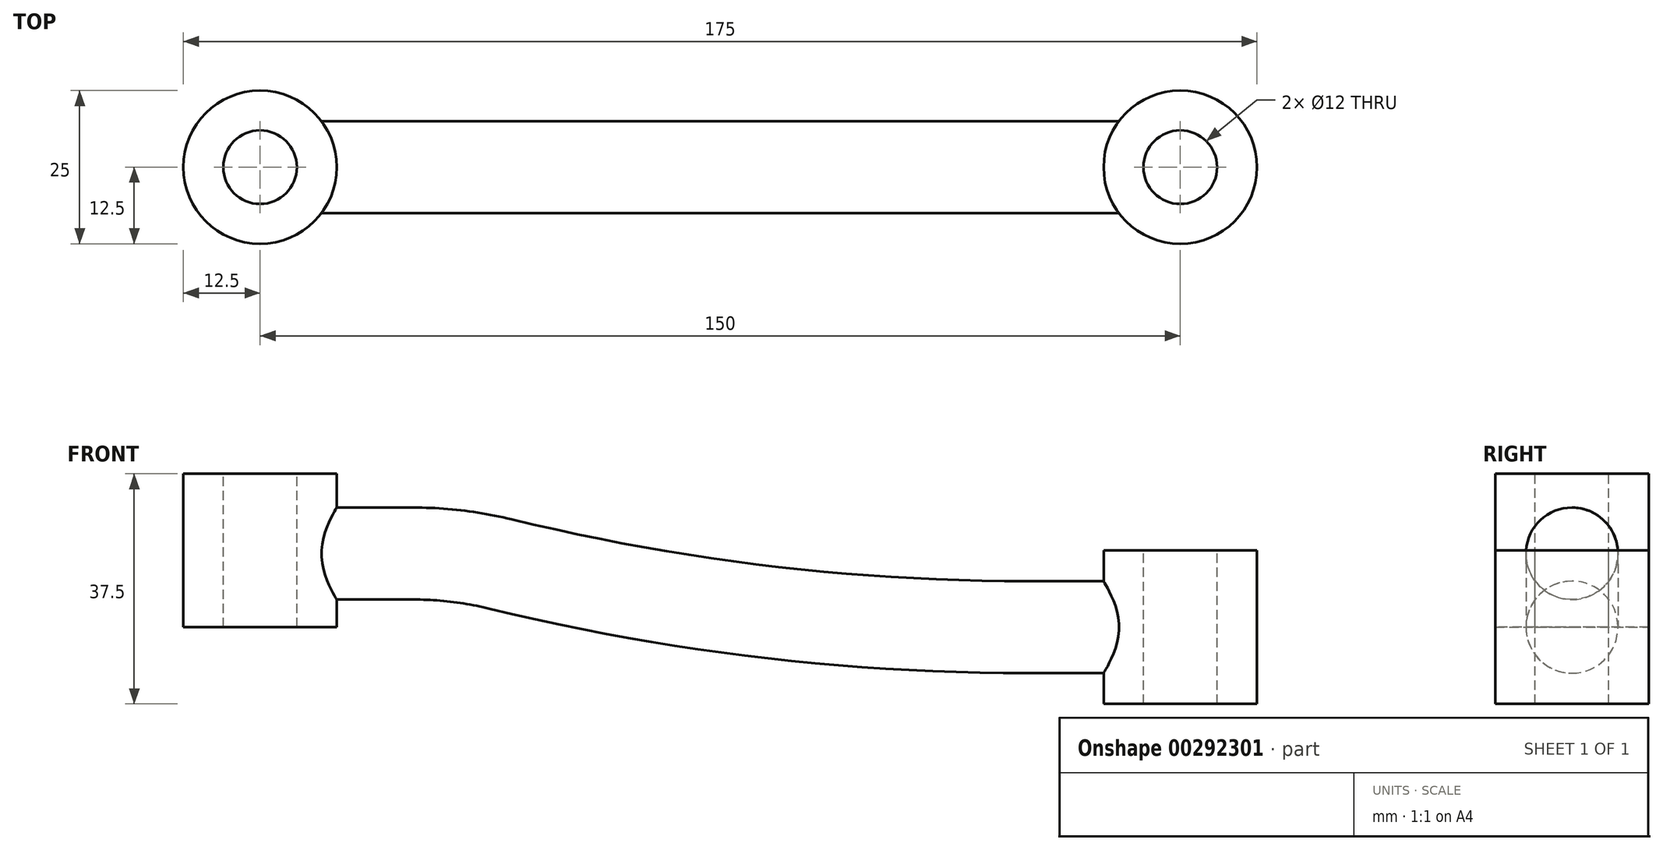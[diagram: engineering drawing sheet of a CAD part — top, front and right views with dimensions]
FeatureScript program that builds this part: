
annotation { "Feature Type Name" : "Feature", "Feature Type Description" : "" }
export const myFeature = defineFeature(function(context is Context, id is Id, definition is map)
    precondition{}
    {
        {
            var Q0;
            Q0=qCreatedBy(makeId("Top.planeOp"),FACE);
            var sketch = newSketch(context, id + "F0", { "sketchPlane" : qUnion([Q0])});
            skCircle(sketch, "E0", {"center": v(0, 0) * mm, "radius": 12.5 * mm});
            skCircle(sketch, "E1", {"center": v(150, 0) * mm, "radius": 12.5 * mm});
            skSolve(sketch);
        }
        {
            var Q0;
            Q0=makeQuery(id+"F0.imprint","IMPRINT",FACE,{"disambiguationData":[TD([[makeQuery(id+"F0.imprint","IMPRINT",EDGE,{"derivedFrom":sQuery(id+"F0.wireOp",EDGE,"E0")}),1.0]])]});
            var Q1;
            Q1=sQuery(id+"F0.wireOp",EDGE,"E0");
            extrude(context, id + "F1", {"entities" : qUnion([Q0]), "surfaceEntities" : qUnion([Q1]), "depth" : 25 * mm});
        }
        {
            var Q0;
            Q0=makeQuery(id+"F0.imprint","IMPRINT",FACE,{"disambiguationData":[TD([[makeQuery(id+"F0.imprint","IMPRINT",EDGE,{"derivedFrom":sQuery(id+"F0.wireOp",EDGE,"E1")}),1.0]])]});
            var Q1;
            Q1=sQuery(id+"F0.wireOp",EDGE,"E1");
            extrude(context, id + "F2", {"entities" : qUnion([Q0]), "surfaceEntities" : qUnion([Q1]), "endBound" : BoundingType.SYMMETRIC, "depth" : 25 * mm});
        }
        {
            var Q0;
            Q0=qCreatedBy(makeId("Front.planeOp"),FACE);
            var sketch = newSketch(context, id + "F3", { "sketchPlane" : qUnion([Q0])});
            skLineSegment(sketch, "E2", {"start": v(0, 12) * mm, "end": v(25, 12) * mm});
            skArc(sketch, "E3", {"start": v(25, 12) * mm, "mid": v(32.15, 11.57) * mm, "end": v(39.2, 10.3) * mm});
            skArc(sketch, "E4", {"start": v(39.2, 10.3) * mm, "mid": v(81.79, 2.58) * mm, "end": v(125, 0) * mm});
            skLineSegment(sketch, "E5", {"start": v(125, 0) * mm, "end": v(150, 0) * mm});
            skSolve(sketch);
        }
        {
            var Q0;
            Q0=qCreatedBy(makeId("Right.planeOp"),FACE);
            var sketch = newSketch(context, id + "F4", { "sketchPlane" : qUnion([Q0])});
            skCircle(sketch, "E6", {"center": v(0, 12) * mm, "radius": 7.5 * mm});
            skSolve(sketch);
        }
        {
            var Q0;
            Q0 = qSketchRegion(id + "F4", true);
            var Q1;
            Q1 = qConstructionFilter(qBodyType(qCreatedBy(id + "F3" ,EDGE), BodyType.WIRE), ConstructionObject.NO);
            sweep(context, id + "F5", {"operationType" : NewBodyOperationType.ADD, "profiles" : qUnion([Q0]), "path" : qUnion([Q1])});
        }
        {
            var Q0;
            Q0=makeQuery(id+"F1.opExtrude","CAP_FACE",FACE,{"disambiguationData":[OSD([sQuery(id+"F0.wireOp",EDGE,"E0")])],"isStart":false});
            var sketch = newSketch(context, id + "F6", { "sketchPlane" : qUnion([Q0])});
            skCircle(sketch, "E7", {"center": v(0, 0) * mm, "radius": 6 * mm});
            skCircle(sketch, "E8", {"center": v(150, 0) * mm, "radius": 6 * mm});
            skSolve(sketch);
        }
        {
            var Q0;
            Q0 = qSketchRegion(id + "F6", true);
            extrude(context, id + "F7", {"entities" : qUnion([Q0]), "operationType" : NewBodyOperationType.REMOVE, "endBound" : BoundingType.THROUGH_ALL, "oppositeDirection" : true, "depth" : 25 * mm});
        }
    });
